# Revit family: Base_Cabinet-Danver-Diagonal_Corner
name_source: partatom
category: Casework
units: mm (PartAtom-declared; Revit-internal decimal feet)

## family parameters
Always vertical = Yes
Cut with Voids When Loaded = No
Room Calculation Point = No
Shared = No
Work Plane-Based = No

## types (2) — shared parameters
Cab Height = 2' - 5 3/4"
Cabinet Material = Metal - Danver - Stainless Steel
Construction Type = 304 Grade Stainless Steel
Default Elevation = 0' - 0"
Door Height = 2' - 5 5/8"
Door Material = Metal - Danver - Stainless Steel
Door Panel Material = Metal - Danver - Stainless Steel
Door Width = 1' - 3 1/2"
Handle Material = Metal - Danver - Chrome Plated Steel
Handle Offset = 0' - 1 7/16"
Keynote = 12 35 28
Manufacturer = Danver Outdoor Kitchens
Product Documentation Link = https://danver.com
Product Name = Corner Upper Cabinet - Danver - Diagonal Door
Product Page URL = https://danver.com
Toe Kick Height = 0' - 4 1/2"
Toe Kick Material = Metal - Danver - Toe Kick
URL = www.danver.com
Version = 2019 - V1.0b

## per-type parameters (varying)
| type | Constraints | Depth | Description | Foot Style | Model | Width |
| 24" Depth | 2 | 2' - 0" | 36"x36" Diagonal Corner Cabinet - 1 Door | Foot : Standard with SS Leg Cover | DCB36 | 2' - 0" |
| 27" Depth | 1 | 2' - 3" | 36"x36"Diagonal Corner Cabinet - 1 Door | Foot : Standard | DCB39 | 2' - 3" |

## geometry (parser evidence)
native form markers: Sweep x12
no freeform markers — native parametric forms only
